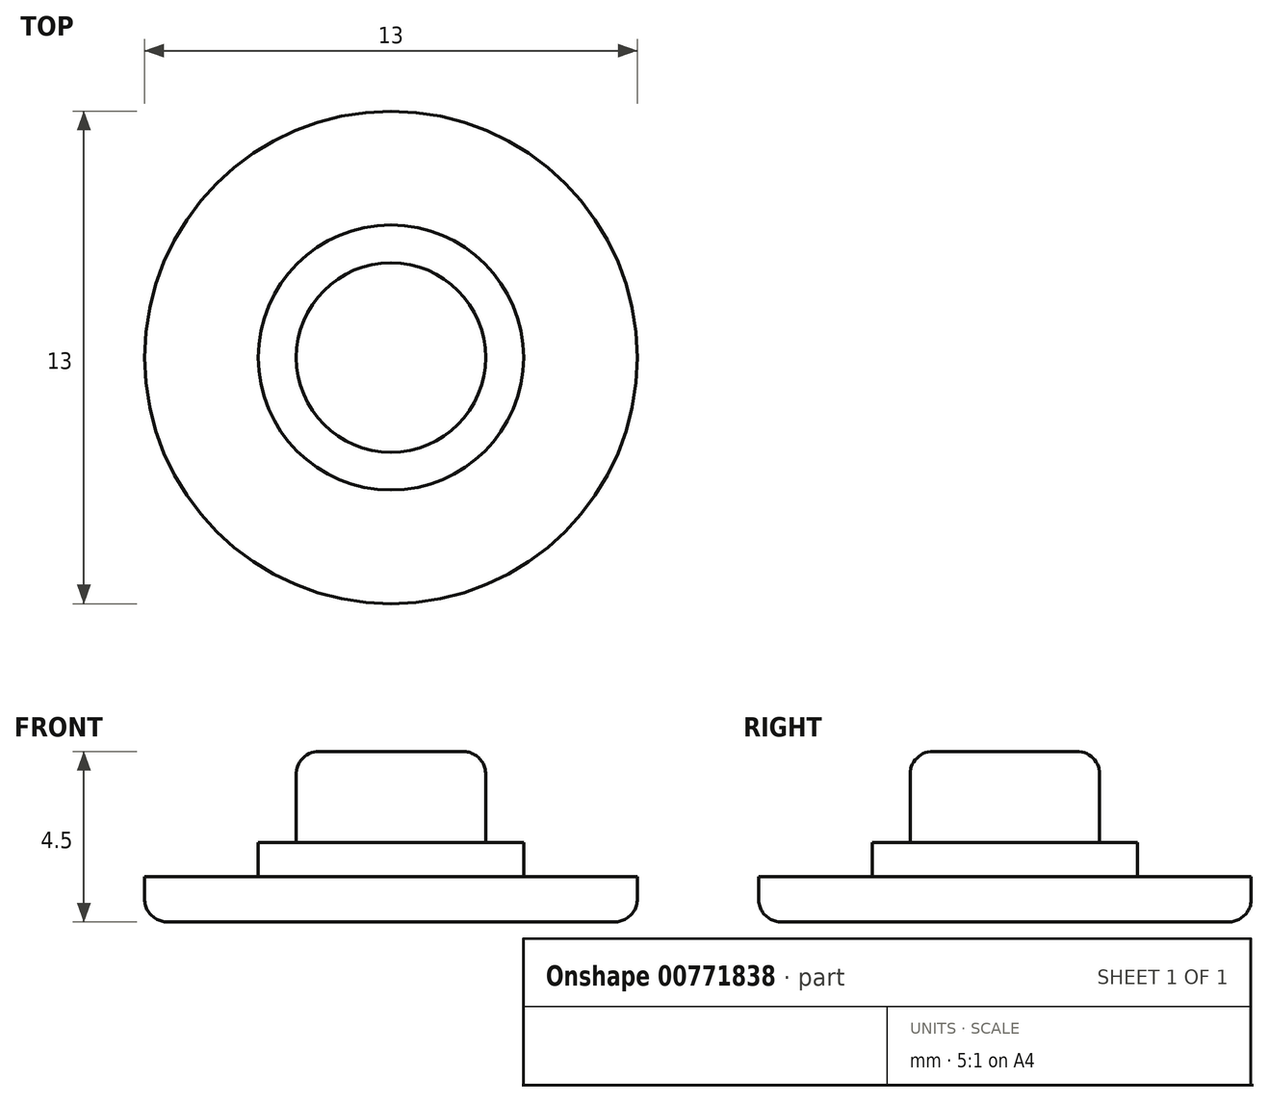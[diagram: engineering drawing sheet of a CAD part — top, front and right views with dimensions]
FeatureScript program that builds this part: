
annotation { "Feature Type Name" : "Feature", "Feature Type Description" : "" }
export const myFeature = defineFeature(function(context is Context, id is Id, definition is map)
    precondition{}
    {
        {
            var Q0;
            Q0=qCreatedBy(makeId("Top.planeOp"),FACE);
            var sketch = newSketch(context, id + "F0", { "sketchPlane" : qUnion([Q0])});
            skCircle(sketch, "E0", {"center": v(0, 0) * mm, "radius": 2.5 * mm});
            skCircle(sketch, "E1.0", {"center": v(0, 0) * mm, "radius": 3.5 * mm});
            skCircle(sketch, "E2", {"center": v(0, 0) * mm, "radius": 6.5 * mm});
            skSolve(sketch);
        }
        {
            assignVariable(context, id + "F1", {"name" : "Capac", "anyValue" : 1.2});
        }
        {
            assignVariable(context, id + "F2", {"name" : "Buza", "anyValue" : 0.9});
        }
        {
            assignVariable(context, id + "F3", {"name" : "Click", "anyValue" : 2.4});
        }
        {
            var Q0;
            Q0=makeQuery(id+"F0.imprint","IMPRINT",FACE,{"disambiguationData":[TD([[makeQuery(id+"F0.imprint","IMPRINT",EDGE,{"derivedFrom":sQuery(id+"F0.wireOp",EDGE,"E1.0")}),-1.0]])]});
            var Q1;
            Q1=makeQuery(id+"F0.imprint","IMPRINT",FACE,{"disambiguationData":[TD([[makeQuery(id+"F0.imprint","IMPRINT",EDGE,{"derivedFrom":sQuery(id+"F0.wireOp",EDGE,"ff67c62d-fdd8-4ad0-9f58-1a85a1549a4c.0")}),-1.0]])]});
            extrude(context, id + "F4", {"entities" : qUnion([Q0, Q1]), "depth" : (getVariable(context, 'Capac')) * mm, "offsetDistance" : 25 * mm});
        }
        {
            var Q0;
            Q0=makeQuery(id+"F0.imprint","IMPRINT",FACE,{"disambiguationData":[TD([[makeQuery(id+"F0.imprint","IMPRINT",EDGE,{"derivedFrom":sQuery(id+"F0.wireOp",EDGE,"E0")}),-1.0]])]});
            var Q1;
            Q1=makeQuery(id+"F0.imprint","IMPRINT",FACE,{"disambiguationData":[TD([[makeQuery(id+"F0.imprint","IMPRINT",EDGE,{"derivedFrom":sQuery(id+"F0.wireOp",EDGE,"7f896e7d-3f19-49c2-ab0c-eae47a83b49e")}),-1.0]])]});
            extrude(context, id + "F5", {"entities" : qUnion([Q0, Q1]), "operationType" : NewBodyOperationType.ADD, "depth" : (getVariable(context, 'Capac') + getVariable(context, 'Buza')) * mm, "offsetDistance" : 25 * mm});
        }
        {
            var Q0;
            Q0=makeQuery(id+"F0.imprint","IMPRINT",FACE,{"disambiguationData":[TD([[makeQuery(id+"F0.imprint","IMPRINT",EDGE,{"derivedFrom":sQuery(id+"F0.wireOp",EDGE,"E0")}),1.0]])]});
            var Q1;
            Q1=makeQuery(id+"F0.imprint","IMPRINT",FACE,{"disambiguationData":[TD([[makeQuery(id+"F0.imprint","IMPRINT",EDGE,{"derivedFrom":sQuery(id+"F0.wireOp",EDGE,"7f896e7d-3f19-49c2-ab0c-eae47a83b49e")}),1.0]])]});
            extrude(context, id + "F6", {"entities" : qUnion([Q0, Q1]), "operationType" : NewBodyOperationType.ADD, "depth" : (getVariable(context, 'Capac') + getVariable(context, 'Buza') + getVariable(context, 'Click')) * mm, "offsetDistance" : 25 * mm});
        }
        {
            var Q0;
            Q0=makeQuery(id+"F6.opExtrude","CAP_FACE",FACE,{"disambiguationData":[OSD([sQuery(id+"F0.wireOp",EDGE,"E0")])],"isStart":false});
            var Q1;
            Q1=makeQuery(id+"F4.opExtrude","CAP_EDGE",EDGE,{"disambiguationData":[OSD([sQuery(id+"F0.wireOp",EDGE,"E2")])],"isStart":true});
            fillet(context, id + "F7", {"entities" : qUnion([Q0, Q1]), "radius" : 0.6 * mm, "tangentPropagation" : true, "allowEdgeOverflow" : false});
        }
    });
